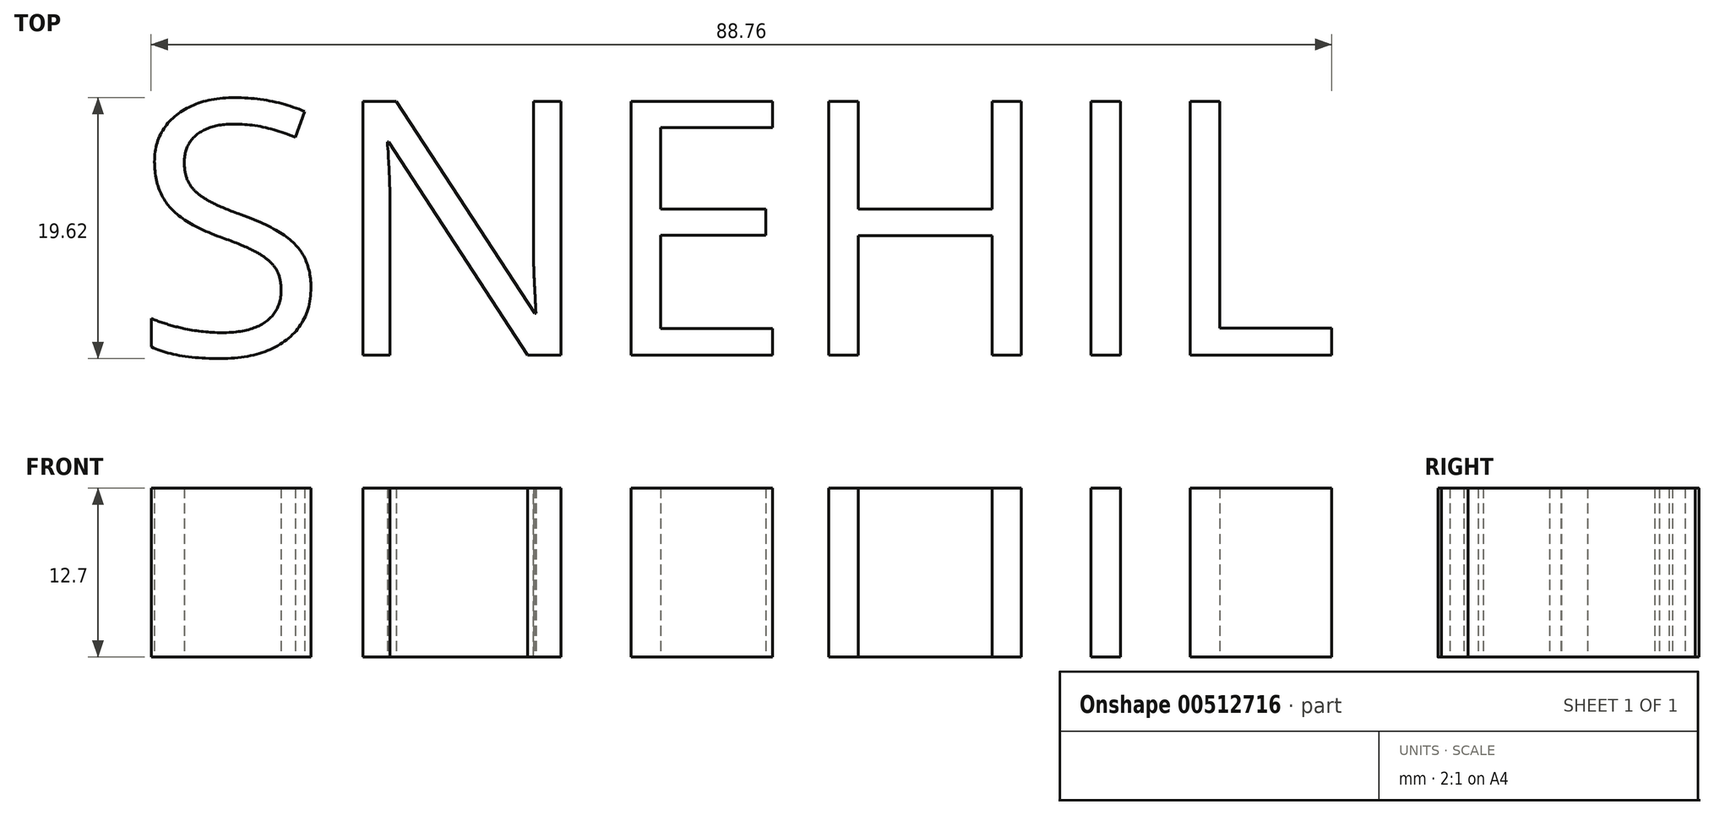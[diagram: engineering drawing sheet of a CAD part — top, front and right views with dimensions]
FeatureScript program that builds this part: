
annotation { "Feature Type Name" : "Feature", "Feature Type Description" : "" }
export const myFeature = defineFeature(function(context is Context, id is Id, definition is map)
    precondition{}
    {
        {
            var Q0;
            Q0=qCreatedBy(makeId("Top.planeOp"),FACE);
            var sketch = newSketch(context, id + "F0", { "sketchPlane" : qUnion([Q0])});
            skText(sketch, "E0", { "text": "SNEHIL", "fontName": "OpenSans-Regular.ttf"});
            const initialGuessF0  = {"E0": [-0.04595, 0.03135, 1, 0, 0.01925]};
            skSetInitialGuess(sketch, initialGuessF0);
            skSolve(sketch);
        }
        {
            var Q0;
            Q0 = qSketchRegion(id + "F0", true);
            extrude(context, id + "F1", {"entities" : qUnion([Q0]), "depth" : 12.7 * mm});
        }
    });
